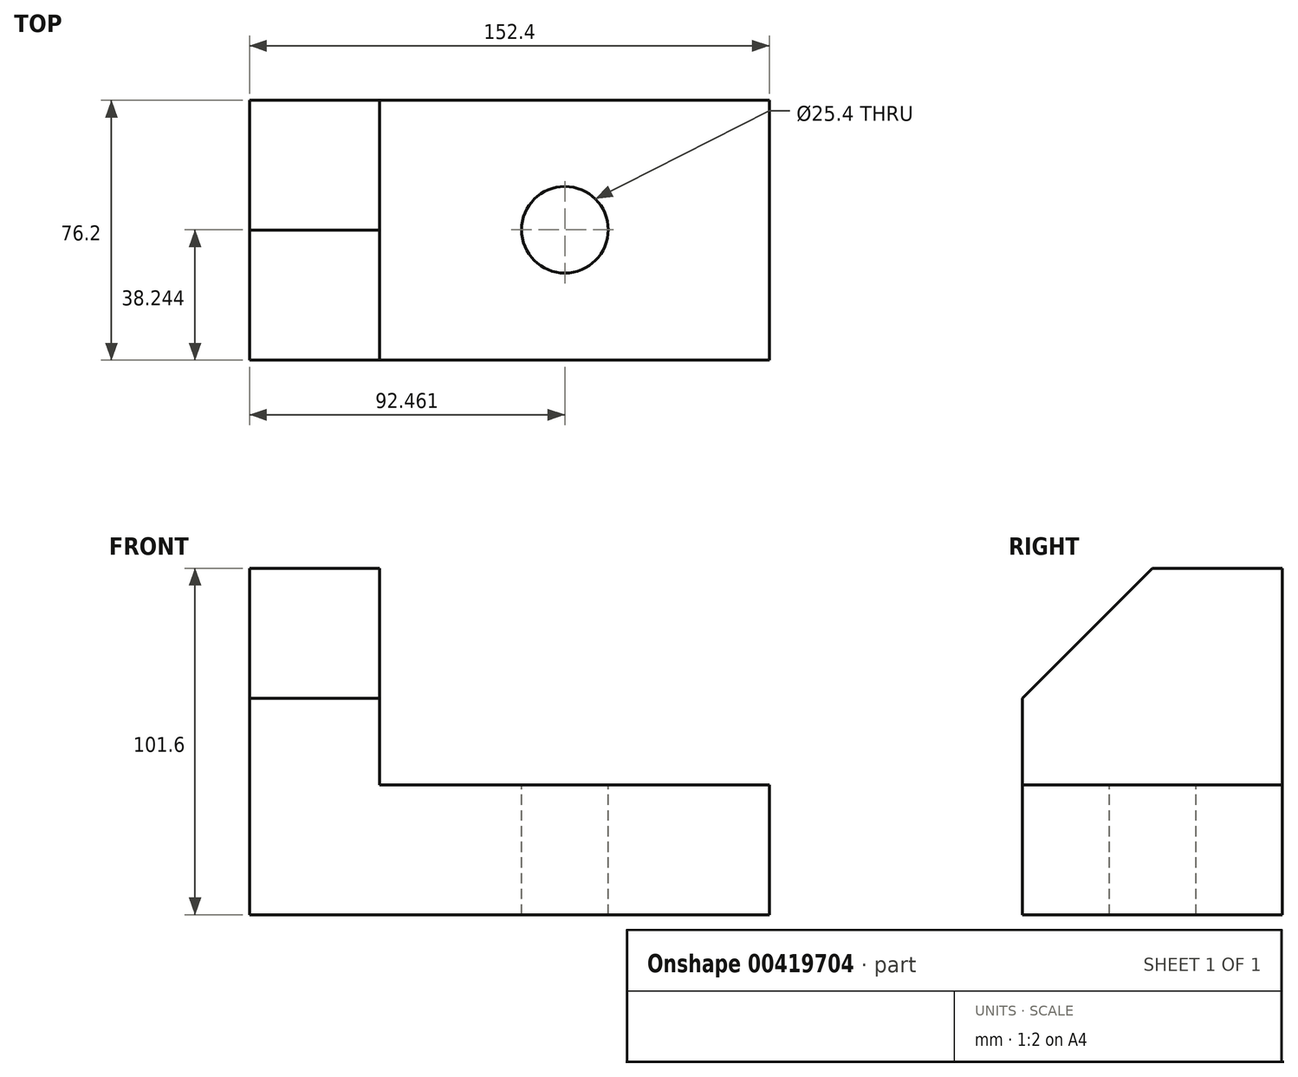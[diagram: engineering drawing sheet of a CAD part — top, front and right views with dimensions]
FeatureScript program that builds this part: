
annotation { "Feature Type Name" : "Feature", "Feature Type Description" : "" }
export const myFeature = defineFeature(function(context is Context, id is Id, definition is map)
    precondition{}
    {
        {
            var Q0;
            Q0=qCreatedBy(makeId("Front.planeOp"),FACE);
            var sketch = newSketch(context, id + "F0", { "sketchPlane" : qUnion([Q0])});
            skLineSegment(sketch, "E0", {"start": v(-152.4, 101.6) * mm, "end": v(-114.3, 101.6) * mm});
            skLineSegment(sketch, "E1", {"start": v(-114.3, 101.6) * mm, "end": v(-114.3, 38.1) * mm});
            skLineSegment(sketch, "E2", {"start": v(-114.3, 38.1) * mm, "end": v(0, 38.1) * mm});
            skLineSegment(sketch, "E3", {"start": v(0, 38.1) * mm, "end": v(0, 0) * mm});
            skLineSegment(sketch, "E4", {"start": v(-152.4, 0) * mm, "end": v(0, 0) * mm});
            skLineSegment(sketch, "E5", {"start": v(-152.4, 101.6) * mm, "end": v(-152.4, 0) * mm});
            skSolve(sketch);
        }
        {
            var Q0;
            Q0=makeQuery(id+"F0.imprint","IMPRINT",FACE,{"disambiguationData":[TD([[makeQuery(id+"F0.imprint","IMPRINT",EDGE,{"derivedFrom":sQuery(id+"F0.wireOp",EDGE,"E0")}),-1.0]])]});
            extrude(context, id + "F1", {"entities" : qUnion([Q0]), "depth" : 76.2 * mm});
        }
        {
            var Q0;
            Q0=makeQuery(id+"F1.opExtrude","SWEPT_FACE",FACE,{"disambiguationData":[OSD([sQuery(id+"F0.wireOp",EDGE,"E1")])]});
            var sketch = newSketch(context, id + "F2", { "sketchPlane" : qUnion([Q0])});
            skLineSegment(sketch, "E6", {"start": v(-38.1, 101.6) * mm, "end": v(-76.2, 63.5) * mm});
            skSolve(sketch);
        }
        {
            var Q0;
            {var subQ0=sQuery(id+"F2.wireOp",EDGE,"E6");Q0=makeQuery(id+"F2.imprint","IMPRINT",FACE,{"disambiguationData":[TD([[makeQuery(id+"F2.imprint","IMPRINT",EDGE,{"derivedFrom":subQ0}),-1.0]])]});}
            extrude(context, id + "F3", {"entities" : qUnion([Q0]), "operationType" : NewBodyOperationType.REMOVE, "endBound" : BoundingType.THROUGH_ALL, "oppositeDirection" : true, "depth" : 25.4 * mm});
        }
        {
            var Q0;
            Q0=makeQuery(id+"F1.opExtrude","SWEPT_FACE",FACE,{"disambiguationData":[OSD([sQuery(id+"F0.wireOp",EDGE,"E2")])]});
            var sketch = newSketch(context, id + "F4", { "sketchPlane" : qUnion([Q0])});
            skCircle(sketch, "E7", {"center": v(-59.94, -37.96) * mm, "radius": 12.7 * mm});
            skSolve(sketch);
        }
        {
            var Q0;
            Q0=makeQuery(id+"F4.imprint","IMPRINT",FACE,{"disambiguationData":[TD([[makeQuery(id+"F4.imprint","IMPRINT",EDGE,{"derivedFrom":sQuery(id+"F4.wireOp",EDGE,"E7")}),1.0]])]});
            extrude(context, id + "F5", {"entities" : qUnion([Q0]), "operationType" : NewBodyOperationType.REMOVE, "endBound" : BoundingType.THROUGH_ALL, "oppositeDirection" : true, "depth" : 25.4 * mm});
        }
    });
